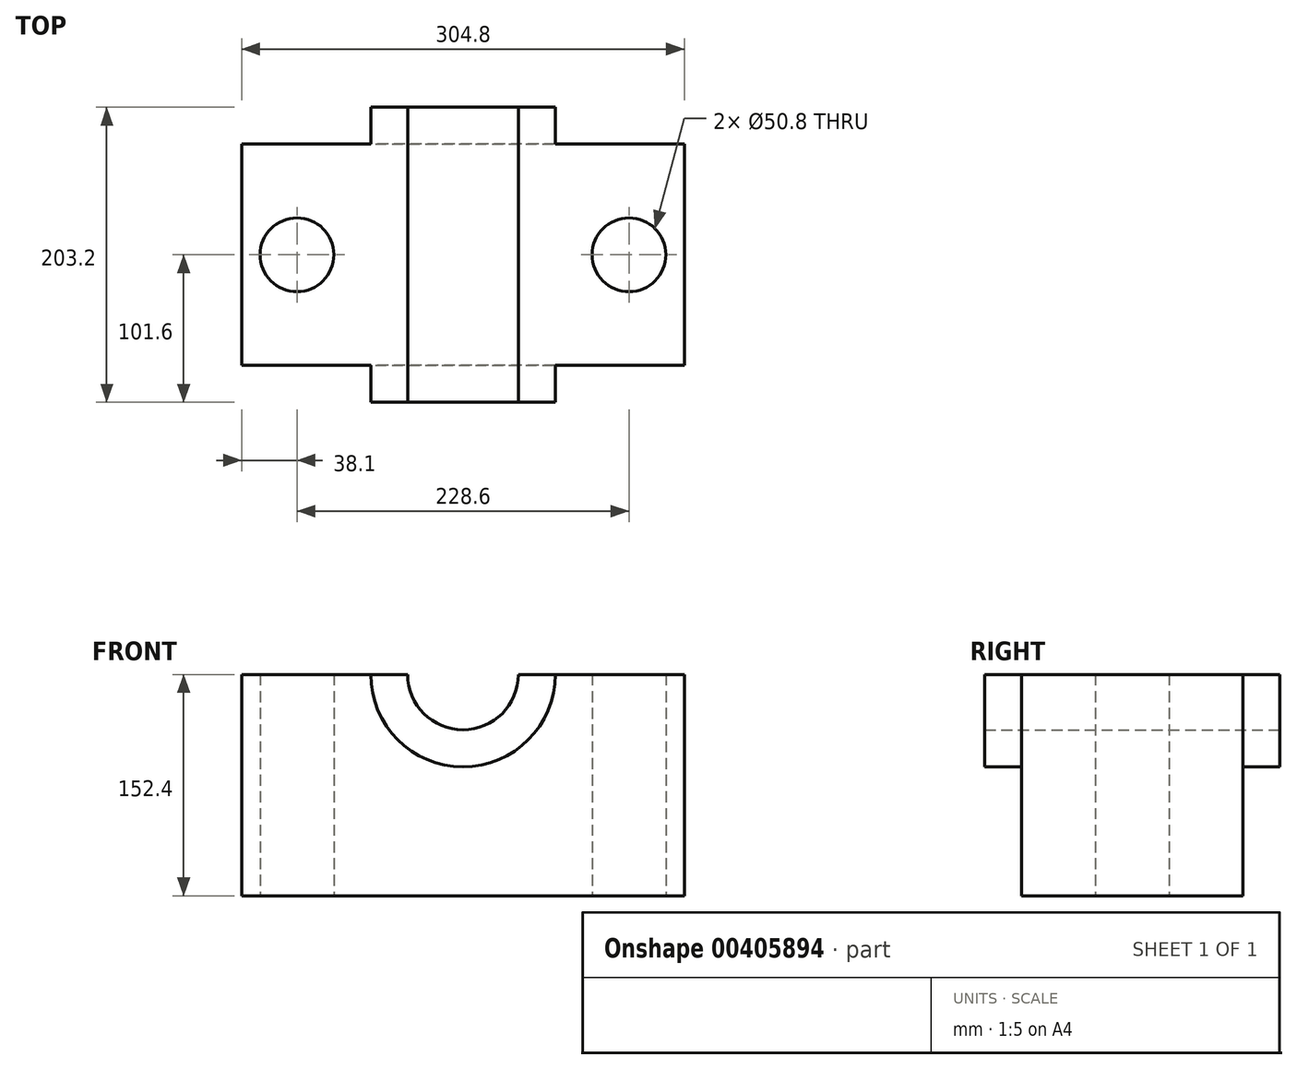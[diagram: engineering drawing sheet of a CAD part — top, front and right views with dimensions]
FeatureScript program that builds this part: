
annotation { "Feature Type Name" : "Feature", "Feature Type Description" : "" }
export const myFeature = defineFeature(function(context is Context, id is Id, definition is map)
    precondition{}
    {
        {
            var Q0;
            Q0=qCreatedBy(makeId("Top.planeOp"),FACE);
            var sketch = newSketch(context, id + "F0", { "sketchPlane" : qUnion([Q0])});
            skLineSegment(sketch, "E0.bottom", {"start": v(-152.4, 76.2) * mm, "end": v(152.4, 76.2) * mm});
            skLineSegment(sketch, "E0.top", {"start": v(-152.4, -76.2) * mm, "end": v(152.4, -76.2) * mm});
            skLineSegment(sketch, "E0.left", {"start": v(-152.4, 76.2) * mm, "end": v(-152.4, -76.2) * mm});
            skLineSegment(sketch, "E0.right", {"start": v(152.4, 76.2) * mm, "end": v(152.4, -76.2) * mm});
            skPoint(sketch, "E0.middle", {"position": v(0, 0) * mm});
            skCircle(sketch, "E1", {"center": v(-114.3, 0) * mm, "radius": 25.4 * mm});
            skPoint(sketch, "E1.centerSnap0", {"position": v(-152.4, 0) * mm});
            skPoint(sketch, "E2.centerSnap0", {"position": v(152.4, 0) * mm});
            skLineSegment(sketch, "E3", {"start": v(0, 76.2) * mm, "end": v(0, -76.2) * mm, "construction": true});
            skCircle(sketch, "E4.MirrorC", {"center": v(114.3, 0) * mm, "radius": 25.4 * mm});
            skSolve(sketch);
        }
        {
            var Q0;
            Q0=makeQuery(id+"F0.imprint","IMPRINT",FACE,{"disambiguationData":[TD([[makeQuery(id+"F0.imprint","IMPRINT",EDGE,{"derivedFrom":sQuery(id+"F0.wireOp",EDGE,"E0.bottom")}),-1.0]])]});
            extrude(context, id + "F1", {"entities" : qUnion([Q0]), "depth" : 152.4 * mm});
        }
        {
            var Q0;
            Q0=qCreatedBy(makeId("Front.planeOp"),FACE);
            var sketch = newSketch(context, id + "F2", { "sketchPlane" : qUnion([Q0])});
            skCircle(sketch, "E5", {"center": v(0, 152.4) * mm, "radius": 38.1 * mm});
            skCircle(sketch, "E6", {"center": v(0, 152.4) * mm, "radius": 63.5 * mm});
            skLineSegment(sketch, "E7.0", {"start": v(-152.4, 152.4) * mm, "end": v(152.4, 152.4) * mm});
            skSolve(sketch);
        }
        {
            var Q0;
            {var subQ0=sQuery(id+"F2.wireOp",EDGE,"E7.0");var subQ1=sQuery(id+"F2.wireOp",EDGE,"E5");var subQ2=makeQuery(id+"F2.imprint","INTERSECT",VERTEX,{"disambiguationData":[OD(0.0)],"derivedFrom":[subQ1,subQ0]});Q0=makeQuery(id+"F2.imprint","IMPRINT",FACE,{"disambiguationData":[TD([[makeQuery(id+"F2.imprint","IMPRINT",EDGE,{"disambiguationData":[TD([[subQ2,-1.0]])],"derivedFrom":subQ1}),-1.0]])]});}
            extrude(context, id + "F3", {"entities" : qUnion([Q0]), "operationType" : NewBodyOperationType.ADD, "endBound" : BoundingType.SYMMETRIC, "depth" : 203.2 * mm});
        }
        {
            var Q0;
            {var subQ0=sQuery(id+"F0.wireOp",EDGE,"E0.top");var subQ1=sQuery(id+"F2.wireOp",EDGE,"E5");Q0=makeQuery(id+"F3.boolean.opBoolean","SPLIT",FACE,{"disambiguationData":[TD([makeQuery(id+"F3.opExtrude","SWEPT_FACE",FACE,{"disambiguationData":[OSD([subQ1])]})])],"derivedFrom":makeQuery(id+"F1.opExtrude","SWEPT_FACE",FACE,{"disambiguationData":[OSD([subQ0])]})});}
            extrude(context, id + "F4", {"entities" : qUnion([Q0]), "operationType" : NewBodyOperationType.REMOVE, "endBound" : BoundingType.THROUGH_ALL, "oppositeDirection" : true, "depth" : 25.4 * mm});
        }
    });
